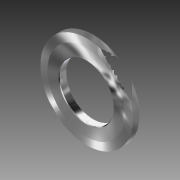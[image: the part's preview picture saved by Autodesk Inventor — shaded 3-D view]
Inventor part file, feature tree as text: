
AUTODESK INVENTOR PART (.ipt)
format: ipt  version: 2014 (Build 180170000, 170)  size: 103,424 bytes
history: native  units: mm (DEFAULTED — no unit token found)
features: chamfer x3, extrude x1, sketch x1
ambient origin geometry x8: Origin, YZ Plane, XZ Plane, XY Plane, X Axis, Y Axis, Z Axis, Center Point
bodies: Solid1 (feature_tree)
feature tree (5):
  extrude  "Extrusion1"  Depth=1.5875mm TaperAngle=0.0deg
  chamfer  "Chamfer1"  Distance=1.5875mm
  chamfer  "Chamfer2"  Distance=1.5875mm
  chamfer  "Chamfer3"  Distance=0.127mm
  sketch  "Sketch1"  dims[d0=11.1125mm d1=1.5875mm d2=0.0mm d3=0.127mm d4=1.5875mm d5=1.5875mm d6=0.127mm d7=0.127mm d8=0.127mm d9=45.0deg d10=45.0deg d11=45.0deg]
